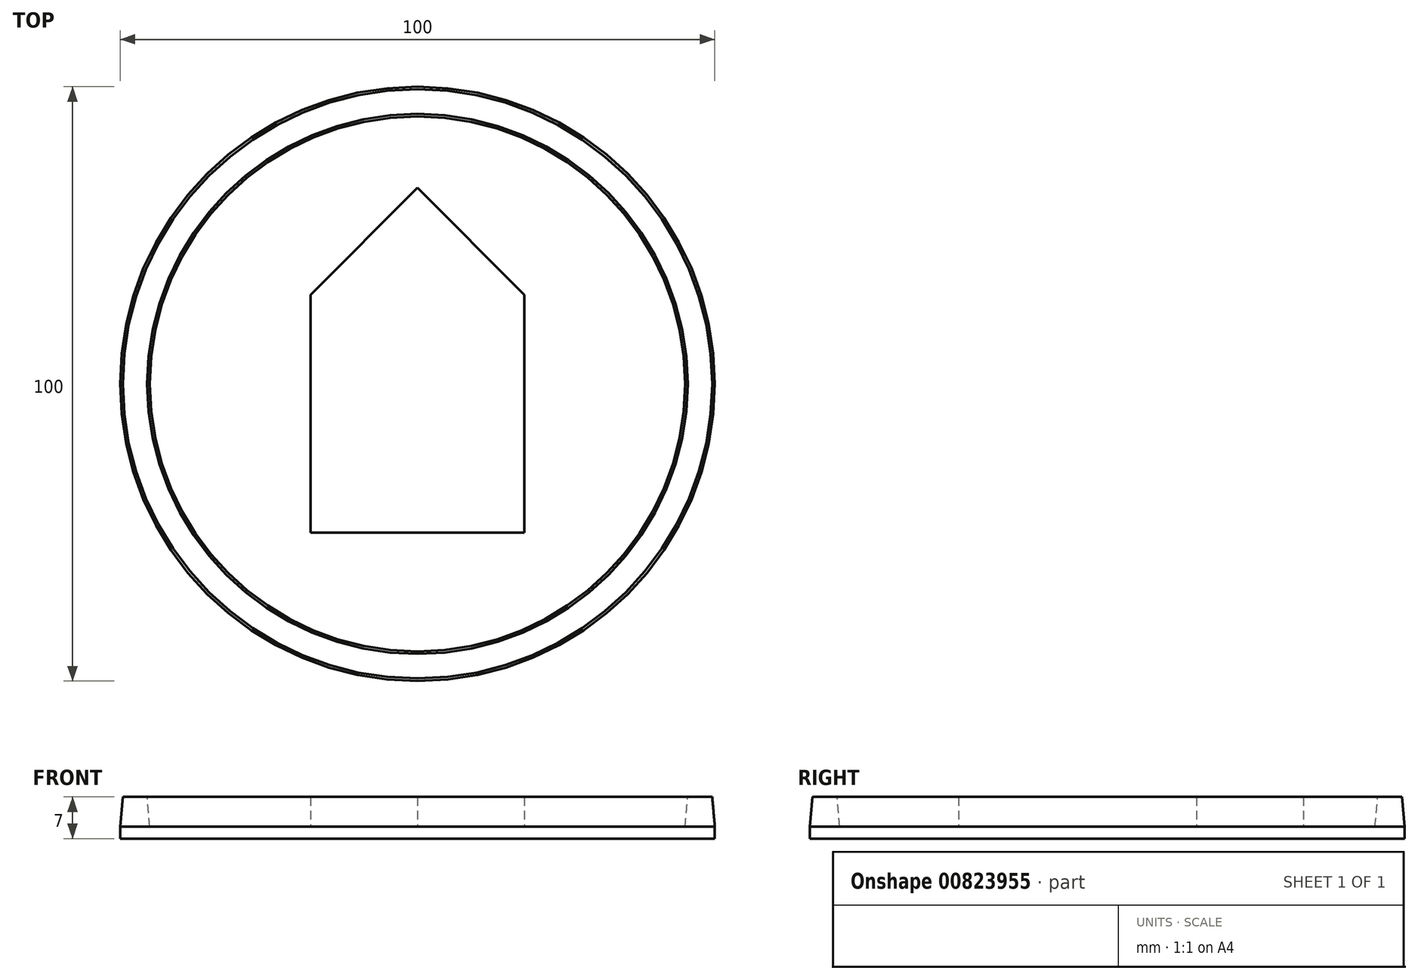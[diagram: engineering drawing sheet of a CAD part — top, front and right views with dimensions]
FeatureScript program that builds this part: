
annotation { "Feature Type Name" : "Feature", "Feature Type Description" : "" }
export const myFeature = defineFeature(function(context is Context, id is Id, definition is map)
    precondition{}
    {
        {
            var Q0;
            Q0=qCreatedBy(makeId("Top.planeOp"),FACE);
            var sketch = newSketch(context, id + "F0", { "sketchPlane" : qUnion([Q0])});
            skCircle(sketch, "E0", {"center": v(0, 0) * mm, "radius": 50 * mm});
            skSolve(sketch);
        }
        {
            var Q0;
            Q0=makeQuery(id+"F0.imprint","IMPRINT",FACE,{"disambiguationData":[TD([[makeQuery(id+"F0.imprint","IMPRINT",EDGE,{"derivedFrom":sQuery(id+"F0.wireOp",EDGE,"E0")}),1.0]])]});
            extrude(context, id + "F1", {"entities" : qUnion([Q0]), "depth" : 2 * mm, "offsetDistance" : 25 * mm});
        }
        {
            var Q0;
            Q0=makeQuery(id+"F1.opExtrude","CAP_FACE",FACE,{"disambiguationData":[OSD([sQuery(id+"F0.wireOp",EDGE,"E0")])],"isStart":false});
            var sketch = newSketch(context, id + "F2", { "sketchPlane" : qUnion([Q0])});
            skCircle(sketch, "E1.0", {"center": v(0, 0) * mm, "radius": 50 * mm});
            skCircle(sketch, "E2", {"center": v(0, 0) * mm, "radius": 45 * mm});
            skSolve(sketch);
        }
        {
            var Q0;
            Q0 = qSketchRegion(id + "F2", true);
            extrude(context, id + "F3", {"entities" : qUnion([Q0]), "operationType" : NewBodyOperationType.ADD, "depth" : 5 * mm, "offsetDistance" : 25 * mm, "hasDraft" : true, "draftAngle" : 5 * degree, "draftPullDirection" : true});
        }
        {
            var Q0;
            Q0=makeQuery(id+"F1.opExtrude","CAP_FACE",FACE,{"disambiguationData":[OSD([sQuery(id+"F0.wireOp",EDGE,"E0")])],"isStart":false});
            var sketch = newSketch(context, id + "F4", { "sketchPlane" : qUnion([Q0])});
            skLineSegment(sketch, "E3", {"start": v(0, -25) * mm, "end": v(-18, -25) * mm});
            skLineSegment(sketch, "E4", {"start": v(-18, -25) * mm, "end": v(-18, 15) * mm});
            skLineSegment(sketch, "E5", {"start": v(-18, 15) * mm, "end": v(0, 33) * mm});
            skLineSegment(sketch, "E6", {"start": v(0, 33) * mm, "end": v(18, 15) * mm});
            skLineSegment(sketch, "E7", {"start": v(18, 15) * mm, "end": v(18, -25) * mm});
            skLineSegment(sketch, "E8", {"start": v(18, -25) * mm, "end": v(0, -25) * mm});
            skSolve(sketch);
        }
        {
            var Q0;
            Q0 = qSketchRegion(id + "F4", true);
            var Q1;
            Q1=makeQuery(id+"F3.opExtrude","CAP_FACE",FACE,{"disambiguationData":[OSD([sQuery(id+"F2.wireOp",EDGE,"E1.0"),sQuery(id+"F2.wireOp",EDGE,"E2")])],"isStart":false});
            extrude(context, id + "F5", {"entities" : qUnion([Q0]), "operationType" : NewBodyOperationType.ADD, "endBound" : BoundingType.UP_TO_SURFACE, "depth" : 25 * mm, "endBoundEntityFace" : qUnion([Q1]), "offsetDistance" : 25 * mm});
        }
    });
